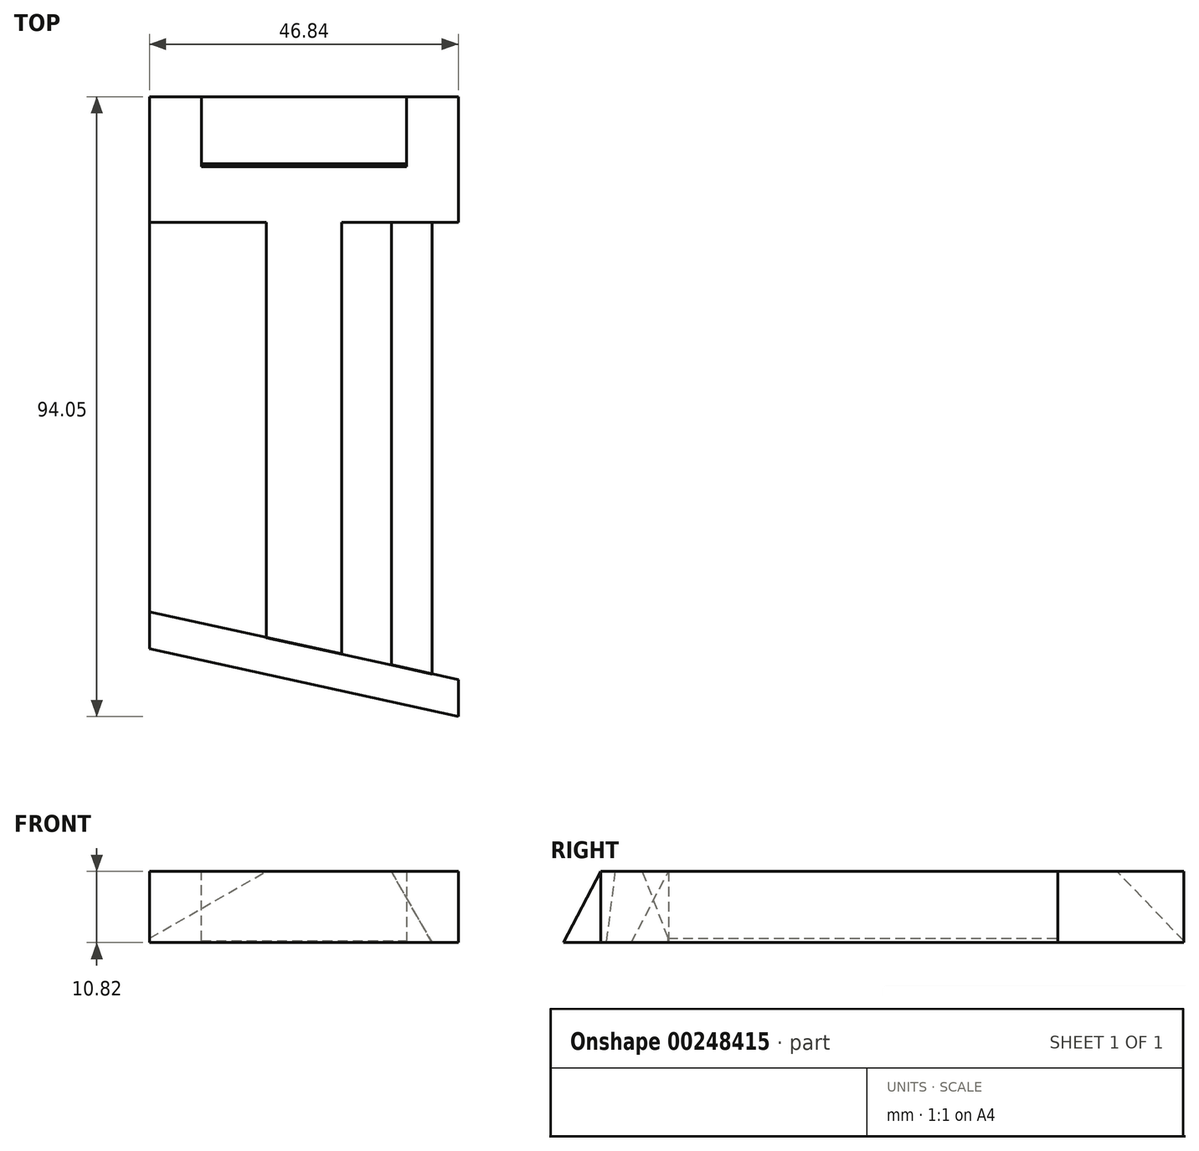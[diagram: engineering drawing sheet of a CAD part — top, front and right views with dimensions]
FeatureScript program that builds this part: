
annotation { "Feature Type Name" : "Feature", "Feature Type Description" : "" }
export const myFeature = defineFeature(function(context is Context, id is Id, definition is map)
    precondition{}
    {
        {
            var Q0;
            Q0=qCreatedBy(makeId("Top.planeOp"),FACE);
            var sketch = newSketch(context, id + "F0", { "sketchPlane" : qUnion([Q0])});
            skLineSegment(sketch, "E0", {"start": v(23.41, 24.81) * mm, "end": v(5.7, 24.81) * mm});
            skLineSegment(sketch, "E1", {"start": v(23.41, 24.81) * mm, "end": v(23.41, 43.88) * mm});
            skLineSegment(sketch, "E2", {"start": v(23.41, 43.88) * mm, "end": v(15.57, 43.88) * mm});
            skLineSegment(sketch, "E3", {"start": v(15.57, 43.88) * mm, "end": v(15.57, 33.24) * mm});
            skLineSegment(sketch, "E4.MirrorCS", {"start": v(-15.57, 43.88) * mm, "end": v(-15.57, 33.24) * mm});
            skLineSegment(sketch, "E5.MirrorCS", {"start": v(-23.41, 43.88) * mm, "end": v(-15.57, 43.88) * mm});
            skLineSegment(sketch, "E6.MirrorCS", {"start": v(-23.41, 24.81) * mm, "end": v(-23.41, 43.88) * mm});
            skLineSegment(sketch, "E7", {"start": v(16.2, 33.24) * mm, "end": v(-15.57, 33.24) * mm});
            skLineSegment(sketch, "E8.trimOffspring", {"start": v(-5.7, 24.81) * mm, "end": v(-23.41, 24.81) * mm});
            skLineSegment(sketch, "E9", {"start": v(23.41, 24.81) * mm, "end": v(23.41, -44.6) * mm});
            skLineSegment(sketch, "E10", {"start": v(-23.41, 24.81) * mm, "end": v(-23.41, -34.36) * mm});
            skLineSegment(sketch, "E11", {"start": v(-23.41, -34.36) * mm, "end": v(23.41, -44.6) * mm});
            skLineSegment(sketch, "E12", {"start": v(5.7, 24.81) * mm, "end": v(5.7, -40.73) * mm});
            skLineSegment(sketch, "E13", {"start": v(-5.7, 24.81) * mm, "end": v(-5.7, -38.24) * mm});
            skLineSegment(sketch, "E14", {"start": v(-15.57, 43.88) * mm, "end": v(15.57, 43.88) * mm});
            skSolve(sketch);
        }
        {
            var Q0;
            Q0=makeQuery(id+"F0.imprint","IMPRINT",FACE,{"disambiguationData":[TD([[makeQuery(id+"F0.imprint","IMPRINT",EDGE,{"derivedFrom":sQuery(id+"F0.wireOp",EDGE,"E0")}),-1.0]])]});
            extrude(context, id + "F1", {"entities" : qUnion([Q0]), "depth" : 10.8 * mm, "offsetDistance" : 25.4 * mm});
        }
        {
            var Q0;
            Q0=makeQuery(id+"F0.imprint","IMPRINT",FACE,{"disambiguationData":[TD([[makeQuery(id+"F0.imprint","IMPRINT",EDGE,{"derivedFrom":sQuery(id+"F0.wireOp",EDGE,"E0")}),1.0]])]});
            var Q1;
            Q1=makeQuery(id+"F0.imprint","IMPRINT",FACE,{"disambiguationData":[TD([[makeQuery(id+"F0.imprint","IMPRINT",EDGE,{"derivedFrom":sQuery(id+"F0.wireOp",EDGE,"E8.trimOffspring")}),1.0]])]});
            var Q2;
            {var subQ0=sQuery(id+"F0.wireOp",EDGE,"E3");Q2=makeQuery(id+"F0.imprint","IMPRINT",FACE,{"disambiguationData":[TD([[makeQuery(id+"F0.imprint","IMPRINT",EDGE,{"derivedFrom":subQ0}),-1.0]])]});}
            extrude(context, id + "F2", {"entities" : qUnion([Q0, Q1, Q2]), "depth" : 10.82 * mm, "offsetDistance" : 25.4 * mm});
        }
        {
            var Q0;
            Q0=makeQuery(id+"F2.opExtrude","CAP_EDGE",EDGE,{"disambiguationData":[OSD([sQuery(id+"F0.wireOp",EDGE,"E10")])],"isStart":false});
            chamfer(context, id + "F3", {"entities" : qUnion([Q0]), "chamferType" : ChamferType.TWO_OFFSETS, "width1" : 17.78 * mm, "oppositeDirection" : false, "width2" : 10.16 * mm, "tangentPropagation" : true});
        }
        {
            var Q0;
            Q0=makeQuery(id+"F2.opExtrude","CAP_EDGE",EDGE,{"disambiguationData":[OSD([sQuery(id+"F0.wireOp",EDGE,"E9")])],"isStart":false});
            chamfer(context, id + "F4", {"entities" : qUnion([Q0]), "chamferType" : ChamferType.TWO_OFFSETS, "width1" : 10.16 * mm, "oppositeDirection" : false, "width2" : 17.78 * mm, "tangentPropagation" : true});
        }
        {
            var Q0;
            Q0=makeQuery(id+"F2.opExtrude","CAP_EDGE",EDGE,{"disambiguationData":[OSD([sQuery(id+"F0.wireOp",EDGE,"E14")])],"isStart":false});
            chamfer(context, id + "F5", {"entities" : qUnion([Q0]), "chamferType" : ChamferType.OFFSET_ANGLE, "width" : 10.16 * mm, "oppositeDirection" : false, "angle" : 46 * degree, "tangentPropagation" : true});
        }
        {
            var Q0;
            Q0=makeQuery(id+"F1.opExtrude","SWEPT_BODY",BODY,{"disambiguationData":[OSD([sQuery(id+"F0.wireOp",EDGE,"E0"),sQuery(id+"F0.wireOp",EDGE,"E1"),sQuery(id+"F0.wireOp",EDGE,"E2"),sQuery(id+"F0.wireOp",EDGE,"E3"),sQuery(id+"F0.wireOp",EDGE,"E4.MirrorCS"),sQuery(id+"F0.wireOp",EDGE,"E5.MirrorCS"),sQuery(id+"F0.wireOp",EDGE,"E6.MirrorCS"),sQuery(id+"F0.wireOp",EDGE,"E7"),sQuery(id+"F0.wireOp",EDGE,"E8.trimOffspring"),sQuery(id+"F0.wireOp",EDGE,"E11"),sQuery(id+"F0.wireOp",EDGE,"E12"),sQuery(id+"F0.wireOp",EDGE,"E13")])]});
            var Q1;
            Q1=makeQuery(id+"F2.opExtrude","SWEPT_BODY",BODY,{"disambiguationData":[OSD([sQuery(id+"F0.wireOp",EDGE,"E8.trimOffspring"),sQuery(id+"F0.wireOp",EDGE,"E10"),sQuery(id+"F0.wireOp",EDGE,"E11"),sQuery(id+"F0.wireOp",EDGE,"E13")])]});
            var Q2;
            Q2=makeQuery(id+"F2.opExtrude","SWEPT_BODY",BODY,{"disambiguationData":[OSD([sQuery(id+"F0.wireOp",EDGE,"E0"),sQuery(id+"F0.wireOp",EDGE,"E9"),sQuery(id+"F0.wireOp",EDGE,"E11"),sQuery(id+"F0.wireOp",EDGE,"E12")])]});
            var Q3;
            Q3=makeQuery(id+"F2.opExtrude","SWEPT_BODY",BODY,{"disambiguationData":[OSD([sQuery(id+"F0.wireOp",EDGE,"E3"),sQuery(id+"F0.wireOp",EDGE,"E4.MirrorCS"),sQuery(id+"F0.wireOp",EDGE,"E7"),sQuery(id+"F0.wireOp",EDGE,"E14")])]});
            booleanBodies(context, id + "F6", {"operationType" : BooleanOperationType.UNION, "tools" : qUnion([Q0, Q1, Q2, Q3])});
        }
        {
            var Q0;
            Q0=qCreatedBy(makeId("Top.planeOp"),FACE);
            var sketch = newSketch(context, id + "F7", { "sketchPlane" : qUnion([Q0])});
            skLineSegment(sketch, "E15", {"start": v(-23.42, -34.36) * mm, "end": v(23.4, -44.64) * mm});
            skLineSegment(sketch, "E16", {"start": v(0, -39.5) * mm, "end": v(4.33, -19.77) * mm});
            skSolve(sketch);
        }
        {
            var Q0;
            Q0=sQuery(id+"F7.wireOp",EDGE,"E16");
            cPlane(context, id + "F8", {"entities" : qUnion([Q0]), "cplaneType" : CPlaneType.LINE_ANGLE, "offset" : 25.4 * mm, "angle" : 90 * degree, "width" : 152.4 * mm, "height" : 152.4 * mm});
        }
        {
            var Q0;
            Q0=qCreatedBy(id+"F8.planeOp",FACE);
            var sketch = newSketch(context, id + "F9", { "sketchPlane" : qUnion([Q0])});
            skLineSegment(sketch, "E17", {"start": v(-38.5, 0) * mm, "end": v(-44, 0) * mm});
            skLineSegment(sketch, "E18", {"start": v(-44, 0) * mm, "end": v(-38.5, 10.8) * mm});
            skLineSegment(sketch, "E19", {"start": v(-38.5, 10.8) * mm, "end": v(-38.5, 0) * mm});
            skSolve(sketch);
        }
        {
            var Q0;
            Q0 = qSketchRegion(id + "F9", true);
            extrude(context, id + "F10", {"entities" : qUnion([Q0]), "depth" : 50.8 * mm, "offsetDistance" : 25.4 * mm, "symmetric" : true});
        }
        {
            var Q0;
            {var subQ0=sQuery(id+"F0.wireOp",EDGE,"E13");var subQ1=sQuery(id+"F0.wireOp",EDGE,"E11");var subQ2=sQuery(id+"F0.wireOp",EDGE,"E8.trimOffspring");var subQ3=sQuery(id+"F0.wireOp",EDGE,"E7");var subQ4=sQuery(id+"F0.wireOp",EDGE,"E4.MirrorCS");var subQ5=sQuery(id+"F0.wireOp",EDGE,"E3");var subQ6=sQuery(id+"F0.wireOp",EDGE,"E12");var subQ7=sQuery(id+"F0.wireOp",EDGE,"E0");Q0=makeQuery(id+"F6.opBoolean","MERGE",FACE,{"derivedFrom":[makeQuery(id+"F1.opExtrude","CAP_FACE",FACE,{"disambiguationData":[OSD([subQ7,sQuery(id+"F0.wireOp",EDGE,"E1"),sQuery(id+"F0.wireOp",EDGE,"E2"),subQ5,subQ4,sQuery(id+"F0.wireOp",EDGE,"E5.MirrorCS"),sQuery(id+"F0.wireOp",EDGE,"E6.MirrorCS"),subQ3,subQ2,subQ1,subQ6,subQ0])],"isStart":true}),makeQuery(id+"F2.opExtrude","CAP_FACE",FACE,{"disambiguationData":[OSD([subQ7,sQuery(id+"F0.wireOp",EDGE,"E9"),subQ1,subQ6])],"isStart":true}),makeQuery(id+"F2.opExtrude","CAP_FACE",FACE,{"disambiguationData":[OSD([subQ5,subQ4,subQ3,sQuery(id+"F0.wireOp",EDGE,"E14")])],"isStart":true}),makeQuery(id+"F2.opExtrude","CAP_FACE",FACE,{"disambiguationData":[OSD([subQ2,sQuery(id+"F0.wireOp",EDGE,"E10"),subQ1,subQ0])],"isStart":true})]});}
            var sketch = newSketch(context, id + "F11", { "sketchPlane" : qUnion([Q0])});
            skLineSegment(sketch, "E20", {"start": v(23.41, 42.08) * mm, "end": v(23.41, 54.1) * mm});
            skLineSegment(sketch, "E21", {"start": v(23.41, 54.1) * mm, "end": v(29.35, 54.1) * mm});
            skLineSegment(sketch, "E22", {"start": v(29.35, 54.1) * mm, "end": v(29.35, 42.08) * mm});
            skLineSegment(sketch, "E23", {"start": v(29.35, 42.08) * mm, "end": v(23.41, 42.08) * mm});
            skLineSegment(sketch, "E24", {"start": v(-23.43, 30.04) * mm, "end": v(-23.43, 44.6) * mm});
            skLineSegment(sketch, "E25", {"start": v(-23.43, 44.6) * mm, "end": v(-29.4, 44.6) * mm});
            skLineSegment(sketch, "E26", {"start": v(-29.4, 44.6) * mm, "end": v(-29.4, 30.04) * mm});
            skLineSegment(sketch, "E27", {"start": v(-29.4, 30.04) * mm, "end": v(-23.43, 30.04) * mm});
            skSolve(sketch);
        }
        {
            var Q0;
            Q0 = qSketchRegion(id + "F11", true);
            extrude(context, id + "F12", {"entities" : qUnion([Q0]), "operationType" : NewBodyOperationType.REMOVE, "oppositeDirection" : true, "depth" : 25.4 * mm, "offsetDistance" : 25.4 * mm, "symmetric" : true});
        }
    });
